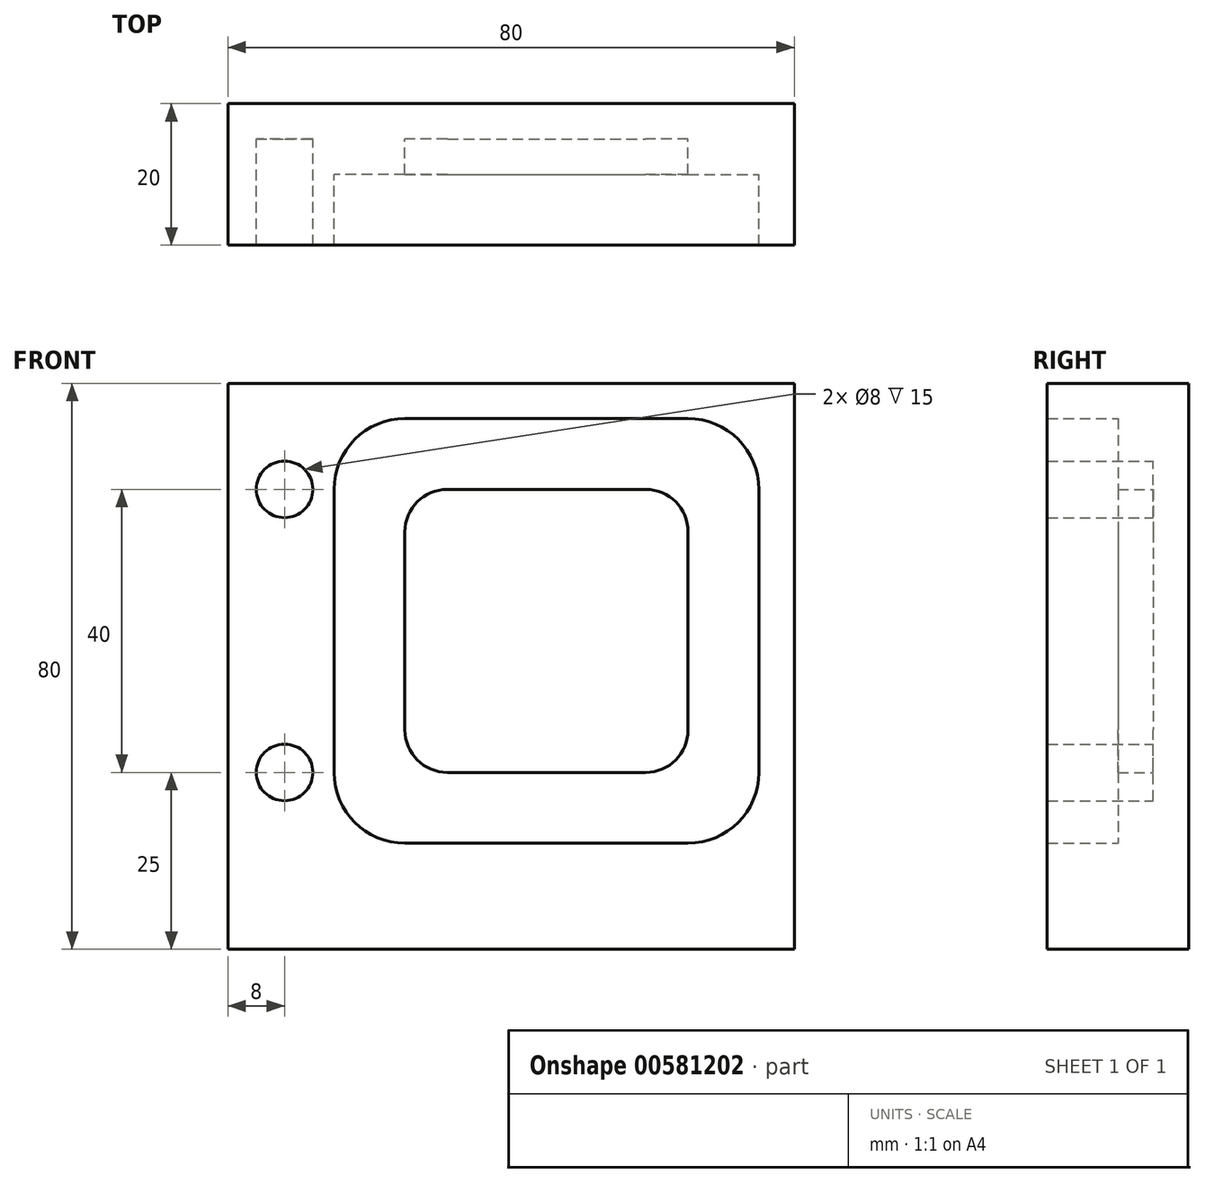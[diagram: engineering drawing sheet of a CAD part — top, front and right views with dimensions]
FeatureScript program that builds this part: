
annotation { "Feature Type Name" : "Feature", "Feature Type Description" : "" }
export const myFeature = defineFeature(function(context is Context, id is Id, definition is map)
    precondition{}
    {
        {
            var Q0;
            Q0=qCreatedBy(makeId("Front.planeOp"),FACE);
            var sketch = newSketch(context, id + "F0", { "sketchPlane" : qUnion([Q0])});
            skLineSegment(sketch, "E0.bottom", {"start": v(0, 0) * mm, "end": v(-80, 0) * mm});
            skLineSegment(sketch, "E0.top", {"start": v(0, 80) * mm, "end": v(-80, 80) * mm});
            skLineSegment(sketch, "E0.left", {"start": v(0, 0) * mm, "end": v(0, 80) * mm});
            skLineSegment(sketch, "E0.right", {"start": v(-80, 0) * mm, "end": v(-80, 80) * mm});
            skLineSegment(sketch, "E1.bottom", {"start": v(-55, 75) * mm, "end": v(-15, 75) * mm});
            skLineSegment(sketch, "E1.top", {"start": v(-55, 15) * mm, "end": v(-15, 15) * mm});
            skLineSegment(sketch, "E1.left", {"start": v(-65, 65) * mm, "end": v(-65, 25) * mm});
            skLineSegment(sketch, "E1.right", {"start": v(-5, 65) * mm, "end": v(-5, 25) * mm});
            skLineSegment(sketch, "E2.bottom", {"start": v(-49, 65) * mm, "end": v(-21, 65) * mm});
            skLineSegment(sketch, "E2.top", {"start": v(-49, 25) * mm, "end": v(-21, 25) * mm});
            skLineSegment(sketch, "E2.left", {"start": v(-55, 59) * mm, "end": v(-55, 31) * mm});
            skLineSegment(sketch, "E2.right", {"start": v(-15, 59) * mm, "end": v(-15, 31) * mm});
            skCircle(sketch, "E3", {"center": v(-72, 65) * mm, "radius": 4 * mm});
            skCircle(sketch, "E4", {"center": v(-72, 25) * mm, "radius": 4 * mm});
            skLineSegment(sketch, "E5", {"start": v(-55, 25) * mm, "end": v(-15, 65) * mm, "construction": true});
            skLineSegment(sketch, "E6", {"start": v(-55, 65) * mm, "end": v(-15, 25) * mm, "construction": true});
            skPoint(sketch, "E7", {"position": v(-35, 45) * mm});
            skLineSegment(sketch, "E8", {"start": v(-65, 15) * mm, "end": v(-5, 75) * mm, "construction": true});
            skLineSegment(sketch, "E9", {"start": v(-65, 75) * mm, "end": v(-5, 15) * mm, "construction": true});
            skPoint(sketch, "E10.visualSharp", {"position": v(-65, 75) * mm});
            skArc(sketch, "E10.filletArc", {"start": v(-55, 75) * mm, "mid": v(-62.07, 72.07) * mm, "end": v(-65, 65) * mm});
            skPoint(sketch, "E11.visualSharp", {"position": v(-5, 75) * mm});
            skArc(sketch, "E11.filletArc", {"start": v(-5, 65) * mm, "mid": v(-7.93, 72.07) * mm, "end": v(-15, 75) * mm});
            skPoint(sketch, "E12.visualSharp", {"position": v(-55, 25) * mm});
            skArc(sketch, "E12.filletArc", {"start": v(-55, 31) * mm, "mid": v(-53.24, 26.76) * mm, "end": v(-49, 25) * mm});
            skArc(sketch, "E13.filletArc", {"start": v(-49, 65) * mm, "mid": v(-53.24, 63.24) * mm, "end": v(-55, 59) * mm});
            skArc(sketch, "E14.filletArc", {"start": v(-15, 59) * mm, "mid": v(-16.76, 63.24) * mm, "end": v(-21, 65) * mm});
            skPoint(sketch, "E15.visualSharp", {"position": v(-15, 25) * mm});
            skArc(sketch, "E15.filletArc", {"start": v(-21, 25) * mm, "mid": v(-16.76, 26.76) * mm, "end": v(-15, 31) * mm});
            skPoint(sketch, "E16.visualSharp", {"position": v(-65, 15) * mm});
            skArc(sketch, "E16.filletArc", {"start": v(-65, 25) * mm, "mid": v(-62.07, 17.93) * mm, "end": v(-55, 15) * mm});
            skPoint(sketch, "E17.visualSharp", {"position": v(-5, 15) * mm});
            skArc(sketch, "E17.filletArc", {"start": v(-15, 15) * mm, "mid": v(-7.93, 17.93) * mm, "end": v(-5, 25) * mm});
            skLineSegment(sketch, "E18", {"start": v(-72, 65) * mm, "end": v(-72, 25) * mm});
            skSolve(sketch);
        }
        {
            var Q0;
            Q0=makeQuery(id+"F0.imprint","IMPRINT",FACE,{"disambiguationData":[TD([[makeQuery(id+"F0.imprint","IMPRINT",EDGE,{"derivedFrom":sQuery(id+"F0.wireOp",EDGE,"E2.bottom")}),-1.0]])]});
            extrude(context, id + "F1", {"entities" : qUnion([Q0]), "depth" : 5 * mm, "offsetDistance" : 25 * mm});
        }
        {
            var Q0;
            Q0=makeQuery(id+"F0.imprint","IMPRINT",FACE,{"disambiguationData":[TD([[makeQuery(id+"F0.imprint","IMPRINT",EDGE,{"derivedFrom":sQuery(id+"F0.wireOp",EDGE,"E1.bottom")}),-1.0]])]});
            extrude(context, id + "F2", {"entities" : qUnion([Q0]), "operationType" : NewBodyOperationType.ADD, "depth" : 10 * mm, "offsetDistance" : 25 * mm});
        }
        {
            var Q0;
            Q0=makeQuery(id+"F0.imprint","IMPRINT",FACE,{"disambiguationData":[TD([[makeQuery(id+"F0.imprint","IMPRINT",EDGE,{"derivedFrom":sQuery(id+"F0.wireOp",EDGE,"E0.bottom")}),-1.0]])]});
            extrude(context, id + "F3", {"entities" : qUnion([Q0]), "operationType" : NewBodyOperationType.ADD, "depth" : 20 * mm, "offsetDistance" : 25 * mm});
        }
        {
            var Q0;
            Q0=makeQuery(id+"F0.imprint","IMPRINT",FACE,{"disambiguationData":[TD([[makeQuery(id+"F0.imprint","IMPRINT",EDGE,{"derivedFrom":sQuery(id+"F0.wireOp",EDGE,"E3")}),1.0]])]});
            var Q1;
            Q1=makeQuery(id+"F0.imprint","IMPRINT",FACE,{"disambiguationData":[TD([[makeQuery(id+"F0.imprint","IMPRINT",EDGE,{"derivedFrom":sQuery(id+"F0.wireOp",EDGE,"E4")}),1.0]])]});
            extrude(context, id + "F4", {"entities" : qUnion([Q0, Q1]), "operationType" : NewBodyOperationType.ADD, "depth" : 5 * mm, "offsetDistance" : 25 * mm});
        }
    });
